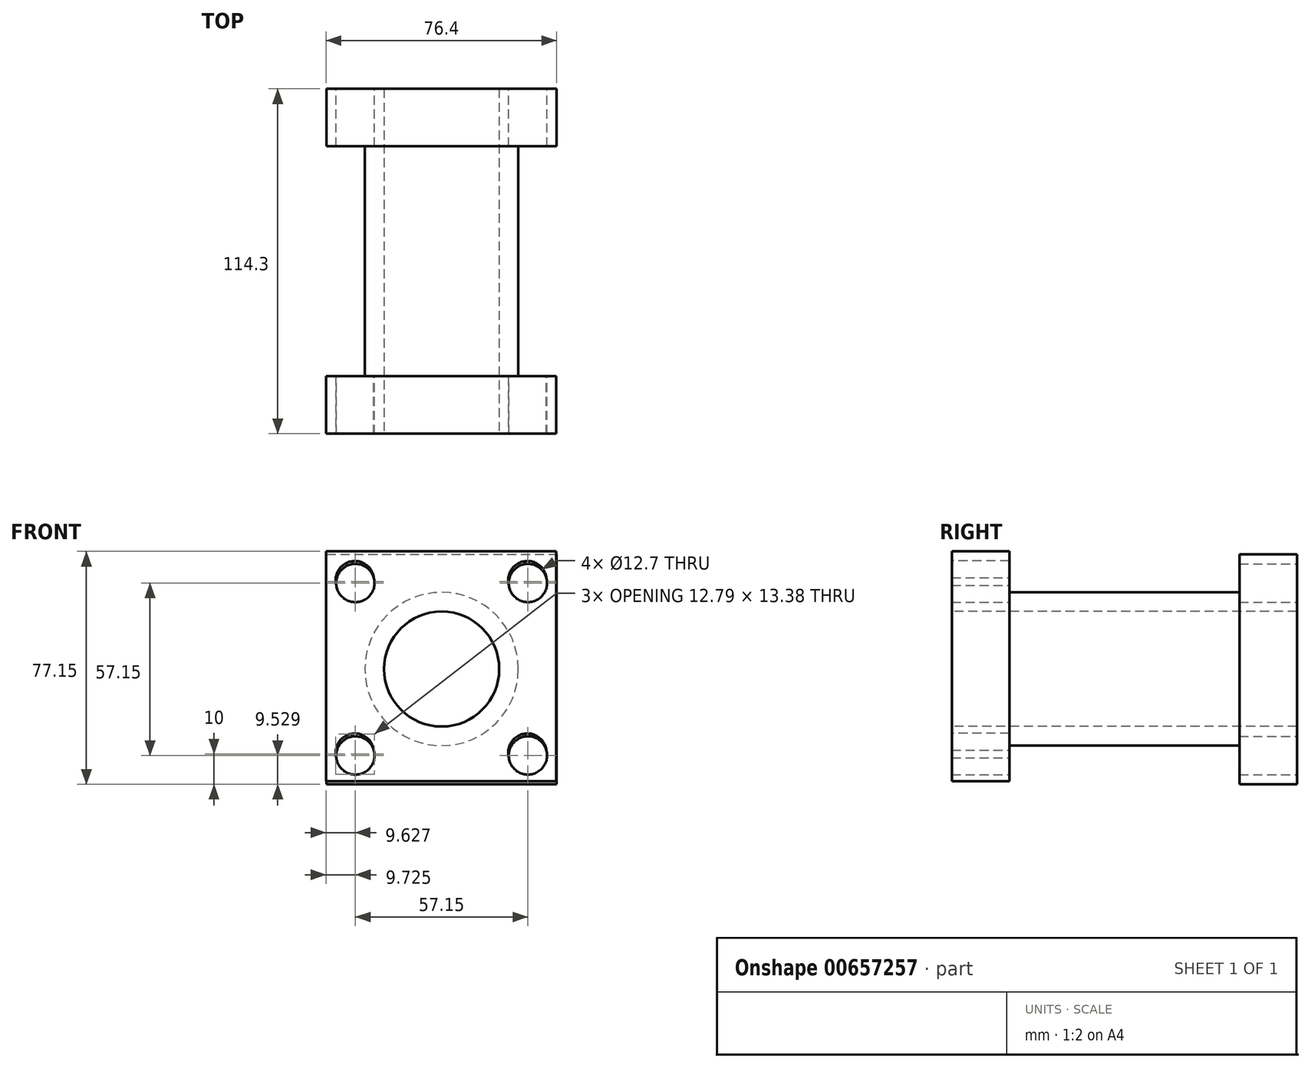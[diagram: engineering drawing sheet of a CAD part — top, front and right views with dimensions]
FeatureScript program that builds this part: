
annotation { "Feature Type Name" : "Feature", "Feature Type Description" : "" }
export const myFeature = defineFeature(function(context is Context, id is Id, definition is map)
    precondition{}
    {
        {
            var Q0;
            Q0=qCreatedBy(makeId("Front.planeOp"),FACE);
            var sketch = newSketch(context, id + "F0", { "sketchPlane" : qUnion([Q0])});
            skLineSegment(sketch, "E0.bottom", {"start": v(-38.1, 38.03) * mm, "end": v(38.1, 38.03) * mm});
            skLineSegment(sketch, "E0.top", {"start": v(-38.1, -38.17) * mm, "end": v(38.1, -38.17) * mm});
            skLineSegment(sketch, "E0.left", {"start": v(-38.1, 38.03) * mm, "end": v(-38.1, -38.17) * mm});
            skLineSegment(sketch, "E0.right", {"start": v(38.1, 38.03) * mm, "end": v(38.1, -38.17) * mm});
            skSolve(sketch);
        }
        {
            var Q0;
            Q0=makeQuery(id+"F0.imprint","IMPRINT",FACE,{"disambiguationData":[TD([[makeQuery(id+"F0.imprint","IMPRINT",EDGE,{"derivedFrom":sQuery(id+"F0.wireOp",EDGE,"E0.bottom")}),-1.0]])]});
            extrude(context, id + "F1", {"entities" : qUnion([Q0]), "depth" : 19.05 * mm, "offsetDistance" : 25.4 * mm});
        }
        {
            var Q0;
            Q0=makeQuery(id+"F1.opExtrude","CAP_FACE",FACE,{"disambiguationData":[OSD([sQuery(id+"F0.wireOp",EDGE,"E0.bottom"),sQuery(id+"F0.wireOp",EDGE,"E0.top"),sQuery(id+"F0.wireOp",EDGE,"E0.left"),sQuery(id+"F0.wireOp",EDGE,"E0.right")])],"isStart":false});
            var sketch = newSketch(context, id + "F2", { "sketchPlane" : qUnion([Q0])});
            skCircle(sketch, "E1", {"center": v(0, 0) * mm, "radius": 25.4 * mm});
            skSolve(sketch);
        }
        {
            var Q0;
            Q0 = qSketchRegion(id + "F2", true);
            extrude(context, id + "F3", {"entities" : qUnion([Q0]), "operationType" : NewBodyOperationType.ADD, "depth" : 76.2 * mm, "offsetDistance" : 25.4 * mm});
        }
        {
            var Q0;
            Q0=makeQuery(id+"F3.opExtrude","CAP_FACE",FACE,{"disambiguationData":[OSD([sQuery(id+"F2.wireOp",EDGE,"E1")])],"isStart":false});
            var sketch = newSketch(context, id + "F4", { "sketchPlane" : qUnion([Q0])});
            skLineSegment(sketch, "E2.bottom", {"start": v(-38.3, 38.98) * mm, "end": v(37.9, 38.98) * mm});
            skLineSegment(sketch, "E2.top", {"start": v(-38.3, -37.22) * mm, "end": v(37.9, -37.22) * mm});
            skLineSegment(sketch, "E2.left", {"start": v(-38.3, 38.98) * mm, "end": v(-38.3, -37.22) * mm});
            skLineSegment(sketch, "E2.right", {"start": v(37.9, 38.98) * mm, "end": v(37.9, -37.22) * mm});
            skSolve(sketch);
        }
        {
            var Q0;
            Q0=makeQuery(id+"F4.imprint","IMPRINT",FACE,{"disambiguationData":[TD([[makeQuery(id+"F4.imprint","IMPRINT",EDGE,{"derivedFrom":sQuery(id+"F4.wireOp",EDGE,"E2.bottom")}),-1.0]])]});
            var sketch = newSketch(context, id + "F5", { "sketchPlane" : qUnion([Q0])});
            skSolve(sketch);
        }
        {
            var Q0;
            Q0=makeQuery(id+"F5.imprint","IMPRINT",FACE,{"disambiguationData":[TD([[makeQuery(id+"F5.imprint","IMPRINT",EDGE,{"derivedFrom":makeQuery(id+"F4.imprint","IMPRINT",EDGE,{"derivedFrom":sQuery(id+"F4.wireOp",EDGE,"E2.bottom")})}),-1.0]])]});
            var Q1;
            Q1=makeQuery(id+"F4.imprint","IMPRINT",FACE,{"disambiguationData":[TD([[makeQuery(id+"F4.imprint","IMPRINT",EDGE,{"derivedFrom":makeQuery(id+"F3.opExtrude","CAP_EDGE",EDGE,{"disambiguationData":[OSD([sQuery(id+"F2.wireOp",EDGE,"E1")])],"isStart":false})}),1.0]])]});
            extrude(context, id + "F6", {"entities" : qUnion([Q0, Q1]), "operationType" : NewBodyOperationType.ADD, "depth" : 19.05 * mm, "offsetDistance" : 25.4 * mm});
        }
        {
            var Q0;
            {var subQ0=sQuery(id+"F2.wireOp",EDGE,"E1");Q0=makeQuery(id+"F6.boolean.opBoolean","MERGE",FACE,{"derivedFrom":[makeQuery(id+"F6.opExtrude","CAP_FACE",FACE,{"disambiguationData":[OSD([subQ0])],"isStart":false}),makeQuery(id+"F6.opExtrude","CAP_FACE",FACE,{"disambiguationData":[OSD([subQ0,sQuery(id+"F4.wireOp",EDGE,"E2.bottom"),sQuery(id+"F4.wireOp",EDGE,"E2.top"),sQuery(id+"F4.wireOp",EDGE,"E2.left"),sQuery(id+"F4.wireOp",EDGE,"E2.right")])],"isStart":false})]});}
            var sketch = newSketch(context, id + "F7", { "sketchPlane" : qUnion([Q0])});
            skLineSegment(sketch, "E3", {"start": v(-38.3, 38.98) * mm, "end": v(37.9, -37.22) * mm});
            skLineSegment(sketch, "E4", {"start": v(37.84, 38.9) * mm, "end": v(-38.3, -37.22) * mm});
            skCircle(sketch, "E5", {"center": v(0, 0) * mm, "radius": 19.05 * mm});
            skSolve(sketch);
        }
        {
            var Q0;
            {var subQ0=sQuery(id+"F7.wireOp",EDGE,"E5");var subQ1=sQuery(id+"F7.wireOp",EDGE,"E3");var subQ2=makeQuery(id+"F7.imprint","INTERSECT",VERTEX,{"disambiguationData":[OD(0.0)],"derivedFrom":[subQ1,subQ0]});Q0=makeQuery(id+"F7.imprint","IMPRINT",FACE,{"disambiguationData":[TD([[makeQuery(id+"F7.imprint","IMPRINT",EDGE,{"disambiguationData":[TD([[subQ2,-1.0]])],"derivedFrom":subQ1}),-1.0]])]});}
            var Q1;
            {var subQ0=sQuery(id+"F7.wireOp",EDGE,"E4");var subQ1=sQuery(id+"F7.wireOp",EDGE,"E3");var subQ2=makeQuery(id+"F7.imprint","INTERSECT",VERTEX,{"derivedFrom":[subQ1,subQ0]});Q1=makeQuery(id+"F7.imprint","IMPRINT",FACE,{"disambiguationData":[TD([[makeQuery(id+"F7.imprint","IMPRINT",EDGE,{"disambiguationData":[TD([[subQ2,-1.0]])],"derivedFrom":subQ1}),-1.0]])]});}
            var Q2;
            {var subQ0=sQuery(id+"F7.wireOp",EDGE,"E4");var subQ1=sQuery(id+"F7.wireOp",EDGE,"E3");var subQ2=makeQuery(id+"F7.imprint","INTERSECT",VERTEX,{"derivedFrom":[subQ1,subQ0]});Q2=makeQuery(id+"F7.imprint","IMPRINT",FACE,{"disambiguationData":[TD([[makeQuery(id+"F7.imprint","IMPRINT",EDGE,{"disambiguationData":[TD([[subQ2,-1.0]])],"derivedFrom":subQ1}),1.0]])]});}
            var Q3;
            {var subQ0=sQuery(id+"F7.wireOp",EDGE,"E5");var subQ1=sQuery(id+"F7.wireOp",EDGE,"E3");var subQ2=makeQuery(id+"F7.imprint","INTERSECT",VERTEX,{"disambiguationData":[OD(0.0)],"derivedFrom":[subQ1,subQ0]});Q3=makeQuery(id+"F7.imprint","IMPRINT",FACE,{"disambiguationData":[TD([[makeQuery(id+"F7.imprint","IMPRINT",EDGE,{"disambiguationData":[TD([[subQ2,-1.0]])],"derivedFrom":subQ1}),1.0]])]});}
            extrude(context, id + "F8", {"entities" : qUnion([Q0, Q1, Q2, Q3]), "operationType" : NewBodyOperationType.REMOVE, "endBound" : BoundingType.THROUGH_ALL, "oppositeDirection" : true, "depth" : 25.4 * mm, "offsetDistance" : 25.4 * mm});
        }
        {
            var Q0;
            {var subQ0=sQuery(id+"F2.wireOp",EDGE,"E1");Q0=makeQuery(id+"F6.boolean.opBoolean","MERGE",FACE,{"derivedFrom":[makeQuery(id+"F6.opExtrude","CAP_FACE",FACE,{"disambiguationData":[OSD([subQ0])],"isStart":false}),makeQuery(id+"F6.opExtrude","CAP_FACE",FACE,{"disambiguationData":[OSD([subQ0,sQuery(id+"F4.wireOp",EDGE,"E2.bottom"),sQuery(id+"F4.wireOp",EDGE,"E2.top"),sQuery(id+"F4.wireOp",EDGE,"E2.left"),sQuery(id+"F4.wireOp",EDGE,"E2.right")])],"isStart":false})]});}
            var sketch = newSketch(context, id + "F9", { "sketchPlane" : qUnion([Q0])});
            skLineSegment(sketch, "E6", {"start": v(-38.3, -37.22) * mm, "end": v(37.9, -37.22) * mm});
            skCircle(sketch, "E7", {"center": v(28.38, 29.45) * mm, "radius": 6.35 * mm});
            skCircle(sketch, "E8", {"center": v(28.38, -27.7) * mm, "radius": 6.35 * mm});
            skCircle(sketch, "E9", {"center": v(-28.77, -27.7) * mm, "radius": 6.35 * mm});
            skCircle(sketch, "E10", {"center": v(-28.77, 29.45) * mm, "radius": 6.35 * mm});
            skSolve(sketch);
        }
        {
            var Q0;
            Q0=makeQuery(id+"F9.imprint","IMPRINT",FACE,{"disambiguationData":[TD([[makeQuery(id+"F9.imprint","IMPRINT",EDGE,{"derivedFrom":sQuery(id+"F9.wireOp",EDGE,"E7")}),1.0]])]});
            var sketch = newSketch(context, id + "F10", { "sketchPlane" : qUnion([Q0])});
            skSolve(sketch);
        }
        {
            var Q0;
            Q0=makeQuery(id+"F9.imprint","IMPRINT",FACE,{"disambiguationData":[TD([[makeQuery(id+"F9.imprint","IMPRINT",EDGE,{"derivedFrom":sQuery(id+"F9.wireOp",EDGE,"E8")}),1.0]])]});
            var Q1;
            Q1=makeQuery(id+"F10.imprint","IMPRINT",FACE,{"disambiguationData":[TD([[makeQuery(id+"F10.imprint","IMPRINT",EDGE,{"derivedFrom":makeQuery(id+"F9.imprint","IMPRINT",EDGE,{"derivedFrom":sQuery(id+"F9.wireOp",EDGE,"E7")})}),1.0]])]});
            var Q2;
            Q2=makeQuery(id+"F9.imprint","IMPRINT",FACE,{"disambiguationData":[TD([[makeQuery(id+"F9.imprint","IMPRINT",EDGE,{"derivedFrom":sQuery(id+"F9.wireOp",EDGE,"E10")}),1.0]])]});
            var Q3;
            Q3=makeQuery(id+"F9.imprint","IMPRINT",FACE,{"disambiguationData":[TD([[makeQuery(id+"F9.imprint","IMPRINT",EDGE,{"derivedFrom":sQuery(id+"F9.wireOp",EDGE,"E9")}),1.0]])]});
            extrude(context, id + "F11", {"entities" : qUnion([Q0, Q1, Q2, Q3]), "operationType" : NewBodyOperationType.REMOVE, "oppositeDirection" : true, "depth" : 25.4 * mm, "offsetDistance" : 25.4 * mm});
        }
        {
            var Q0;
            Q0=makeQuery(id+"F1.opExtrude","CAP_FACE",FACE,{"disambiguationData":[OSD([sQuery(id+"F0.wireOp",EDGE,"E0.bottom"),sQuery(id+"F0.wireOp",EDGE,"E0.top"),sQuery(id+"F0.wireOp",EDGE,"E0.left"),sQuery(id+"F0.wireOp",EDGE,"E0.right")])],"isStart":true});
            var sketch = newSketch(context, id + "F12", { "sketchPlane" : qUnion([Q0])});
            skCircle(sketch, "E11", {"center": v(-28.57, 28.5) * mm, "radius": 6.35 * mm});
            skCircle(sketch, "E12", {"center": v(28.57, 28.5) * mm, "radius": 6.35 * mm});
            skCircle(sketch, "E13", {"center": v(28.57, -28.64) * mm, "radius": 6.35 * mm});
            skCircle(sketch, "E14", {"center": v(-28.58, -28.62) * mm, "radius": 6.35 * mm});
            skSolve(sketch);
        }
        {
            var Q0;
            Q0=makeQuery(id+"F12.imprint","IMPRINT",FACE,{"disambiguationData":[TD([[makeQuery(id+"F12.imprint","IMPRINT",EDGE,{"derivedFrom":sQuery(id+"F12.wireOp",EDGE,"E13")}),1.0]])]});
            var Q1;
            Q1=makeQuery(id+"F12.imprint","IMPRINT",FACE,{"disambiguationData":[TD([[makeQuery(id+"F12.imprint","IMPRINT",EDGE,{"derivedFrom":sQuery(id+"F12.wireOp",EDGE,"E12")}),1.0]])]});
            var Q2;
            Q2=makeQuery(id+"F12.imprint","IMPRINT",FACE,{"disambiguationData":[TD([[makeQuery(id+"F12.imprint","IMPRINT",EDGE,{"derivedFrom":sQuery(id+"F12.wireOp",EDGE,"E11")}),1.0]])]});
            var Q3;
            Q3=makeQuery(id+"F12.imprint","IMPRINT",FACE,{"disambiguationData":[TD([[makeQuery(id+"F12.imprint","IMPRINT",EDGE,{"derivedFrom":sQuery(id+"F12.wireOp",EDGE,"E14")}),1.0]])]});
            extrude(context, id + "F13", {"entities" : qUnion([Q0, Q1, Q2, Q3]), "operationType" : NewBodyOperationType.REMOVE, "endBound" : BoundingType.THROUGH_ALL, "oppositeDirection" : true, "depth" : 25.4 * mm, "offsetDistance" : 25.4 * mm});
        }
    });
